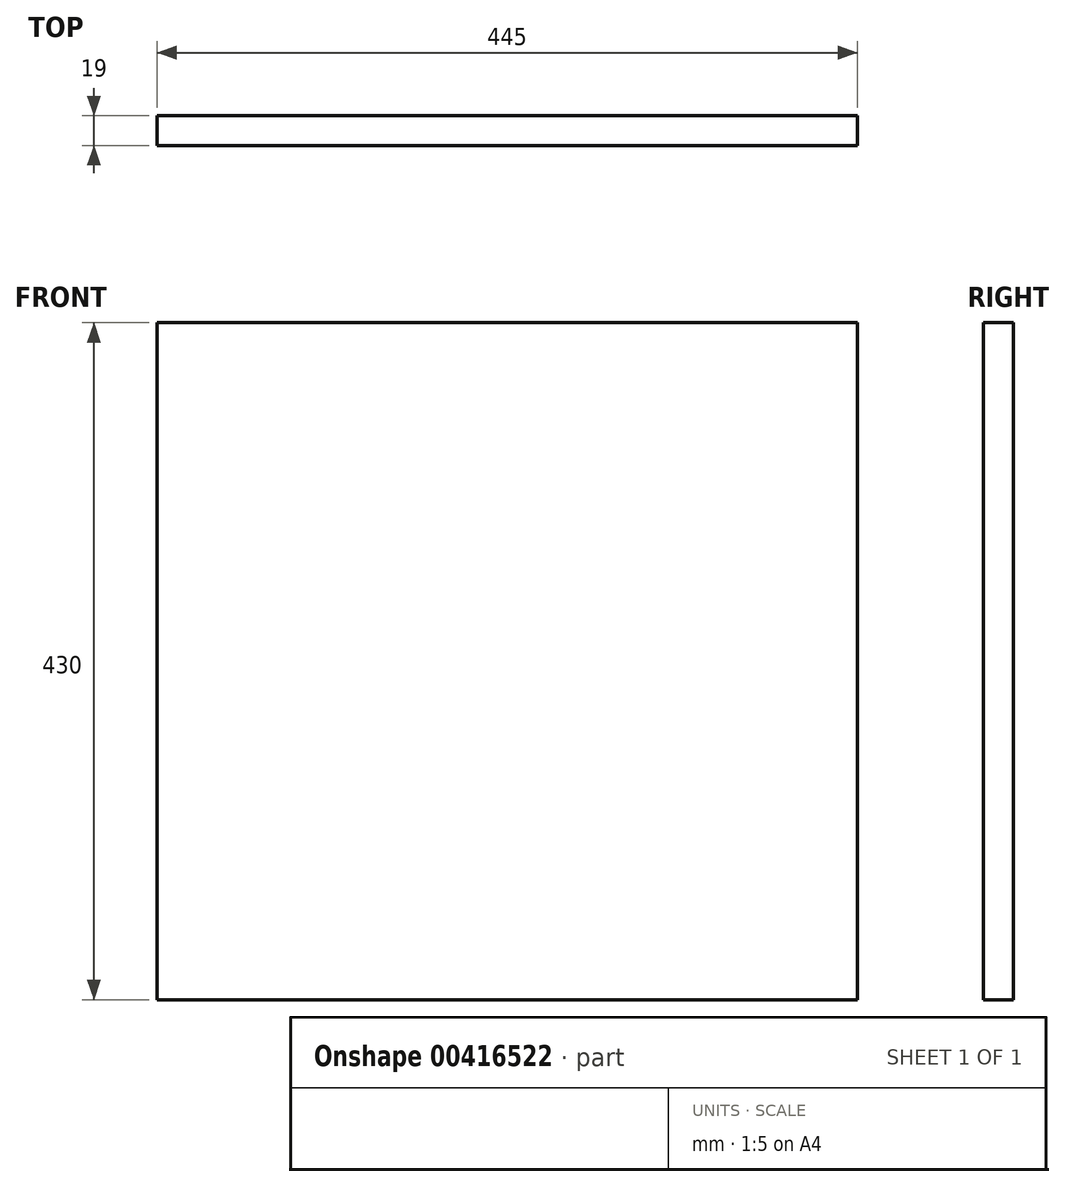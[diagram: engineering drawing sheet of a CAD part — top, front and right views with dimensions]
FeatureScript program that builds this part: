
annotation { "Feature Type Name" : "Feature", "Feature Type Description" : "" }
export const myFeature = defineFeature(function(context is Context, id is Id, definition is map)
    precondition{}
    {
        {
            var Q0;
            Q0=qCreatedBy(makeId("Front.planeOp"),FACE);
            var sketch = newSketch(context, id + "F0", { "sketchPlane" : qUnion([Q0])});
            skLineSegment(sketch, "E0.bottom", {"start": v(-222.5, 215) * mm, "end": v(222.5, 215) * mm});
            skLineSegment(sketch, "E0.top", {"start": v(-222.5, -215) * mm, "end": v(222.5, -215) * mm});
            skLineSegment(sketch, "E0.left", {"start": v(-222.5, 215) * mm, "end": v(-222.5, -215) * mm});
            skLineSegment(sketch, "E0.right", {"start": v(222.5, 215) * mm, "end": v(222.5, -215) * mm});
            skPoint(sketch, "E0.middle", {"position": v(0, 0) * mm});
            skSolve(sketch);
        }
        {
            var Q0;
            Q0=qSketchRegion(id+"F0",true);
            extrude(context, id + "F1", {"entities" : qUnion([Q0]), "depth" : 19 * mm});
        }
    });
